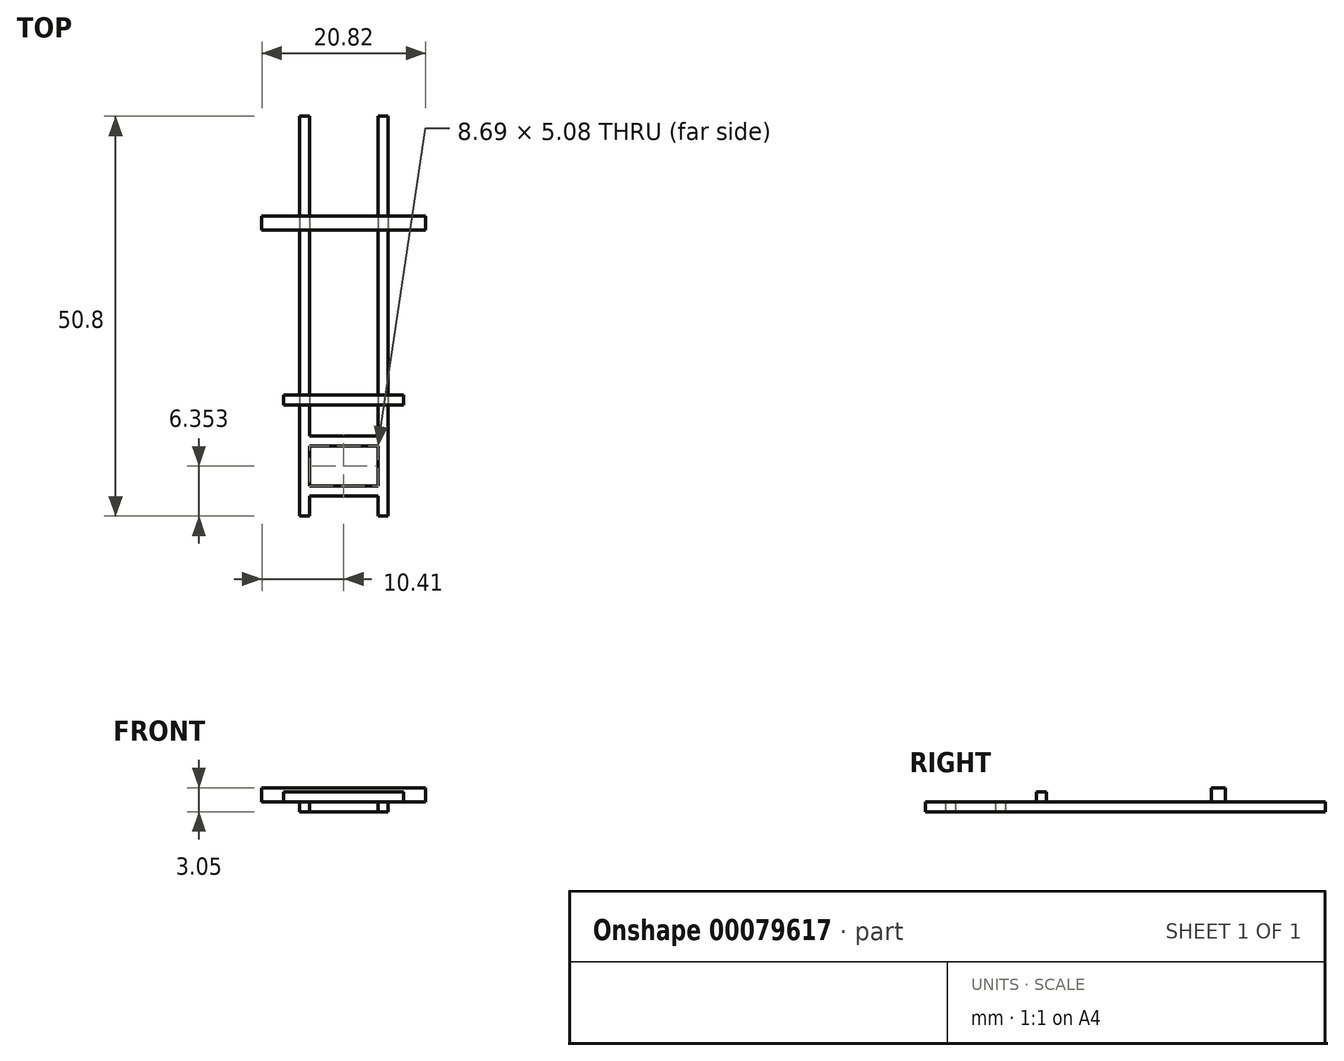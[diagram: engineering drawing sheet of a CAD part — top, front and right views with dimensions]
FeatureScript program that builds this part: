
annotation { "Feature Type Name" : "Feature", "Feature Type Description" : "" }
export const myFeature = defineFeature(function(context is Context, id is Id, definition is map)
    precondition{}
    {
        {
            var Q0;
            Q0=qCreatedBy(makeId("Top.planeOp"),FACE);
            var sketch = newSketch(context, id + "F0", { "sketchPlane" : qUnion([Q0])});
            skLineSegment(sketch, "E0.bottom", {"start": v(-5.61, 6.98) * mm, "end": v(-4.34, 6.98) * mm});
            skLineSegment(sketch, "E0.top", {"start": v(-5.61, -43.82) * mm, "end": v(-4.34, -43.82) * mm});
            skLineSegment(sketch, "E0.left", {"start": v(-5.61, 6.98) * mm, "end": v(-5.61, -43.82) * mm});
            skLineSegment(sketch, "E0.right", {"start": v(-4.34, 6.98) * mm, "end": v(-4.34, -43.82) * mm});
            skLineSegment(sketch, "E1.bottom", {"start": v(4.34, 6.98) * mm, "end": v(5.61, 6.98) * mm});
            skLineSegment(sketch, "E1.top", {"start": v(4.34, -43.82) * mm, "end": v(5.61, -43.82) * mm});
            skLineSegment(sketch, "E1.left", {"start": v(4.34, 6.98) * mm, "end": v(4.34, -43.82) * mm});
            skLineSegment(sketch, "E1.right", {"start": v(5.61, 6.98) * mm, "end": v(5.61, -43.82) * mm});
            skLineSegment(sketch, "E2", {"start": v(-4.34, -41.28) * mm, "end": v(4.34, -41.28) * mm});
            skLineSegment(sketch, "E3", {"start": v(-4.34, -40) * mm, "end": v(4.34, -40) * mm});
            skLineSegment(sketch, "E4", {"start": v(-4.34, -34.93) * mm, "end": v(4.34, -34.93) * mm});
            skLineSegment(sketch, "E5", {"start": v(-4.34, -33.66) * mm, "end": v(4.34, -33.66) * mm});
            skSolve(sketch);
        }
        {
            var Q0;
            Q0 = qSketchRegion(id + "F0", true);
            extrude(context, id + "F1", {"entities" : qUnion([Q0]), "depth" : 1.27 * mm});
        }
        {
            var Q0;
            Q0=makeQuery(id+"F1.opExtrude","CAP_FACE",FACE,{"disambiguationData":[OSD([sQuery(id+"F0.wireOp",EDGE,"E0.bottom"),sQuery(id+"F0.wireOp",EDGE,"E0.top"),sQuery(id+"F0.wireOp",EDGE,"E0.left"),sQuery(id+"F0.wireOp",EDGE,"E0.right"),sQuery(id+"F0.wireOp",EDGE,"E1.bottom"),sQuery(id+"F0.wireOp",EDGE,"E1.top"),sQuery(id+"F0.wireOp",EDGE,"E1.left"),sQuery(id+"F0.wireOp",EDGE,"E1.right"),sQuery(id+"F0.wireOp",EDGE,"E2"),sQuery(id+"F0.wireOp",EDGE,"E3"),sQuery(id+"F0.wireOp",EDGE,"E4"),sQuery(id+"F0.wireOp",EDGE,"E5")])],"isStart":false});
            var sketch = newSketch(context, id + "F2", { "sketchPlane" : qUnion([Q0])});
            skLineSegment(sketch, "E6.bottom", {"start": v(-10.41, -5.72) * mm, "end": v(10.41, -5.72) * mm});
            skLineSegment(sketch, "E6.top", {"start": v(-10.41, -7.5) * mm, "end": v(10.41, -7.5) * mm});
            skLineSegment(sketch, "E6.left", {"start": v(-10.41, -5.72) * mm, "end": v(-10.41, -7.5) * mm});
            skLineSegment(sketch, "E6.right", {"start": v(10.41, -5.72) * mm, "end": v(10.41, -7.5) * mm});
            skSolve(sketch);
        }
        {
            var Q0;
            Q0 = qSketchRegion(id + "F2", true);
            extrude(context, id + "F3", {"entities" : qUnion([Q0]), "operationType" : NewBodyOperationType.ADD, "depth" : 1.78 * mm});
        }
        {
            var Q0;
            {var subQ0=sQuery(id+"F0.wireOp",EDGE,"E1.right");var subQ1=sQuery(id+"F0.wireOp",EDGE,"E3");var subQ2=sQuery(id+"F0.wireOp",EDGE,"E1.left");var subQ3=sQuery(id+"F0.wireOp",EDGE,"E4");var subQ4=sQuery(id+"F0.wireOp",EDGE,"E1.top");var subQ5=sQuery(id+"F0.wireOp",EDGE,"E0.right");var subQ6=sQuery(id+"F0.wireOp",EDGE,"E0.top");var subQ7=sQuery(id+"F0.wireOp",EDGE,"E2");var subQ8=sQuery(id+"F0.wireOp",EDGE,"E1.bottom");var subQ9=sQuery(id+"F0.wireOp",EDGE,"E5");var subQ10=sQuery(id+"F0.wireOp",EDGE,"E0.left");var subQ11=sQuery(id+"F0.wireOp",EDGE,"E0.bottom");Q0=makeQuery(id+"F3.boolean.opBoolean","SPLIT",FACE,{"disambiguationData":[TD([makeQuery(id+"F1.opExtrude","SWEPT_FACE",FACE,{"disambiguationData":[OSD([subQ6])]})])],"derivedFrom":makeQuery(id+"F1.opExtrude","CAP_FACE",FACE,{"disambiguationData":[OSD([subQ11,subQ6,subQ10,subQ5,subQ8,subQ4,subQ2,subQ0,subQ7,subQ1,subQ3,subQ9])],"isStart":false})});}
            var sketch = newSketch(context, id + "F4", { "sketchPlane" : qUnion([Q0])});
            skLineSegment(sketch, "E7.bottom", {"start": v(-7.62, -28.46) * mm, "end": v(7.62, -28.46) * mm});
            skLineSegment(sketch, "E7.top", {"start": v(-7.62, -29.73) * mm, "end": v(7.62, -29.73) * mm});
            skLineSegment(sketch, "E7.left", {"start": v(-7.62, -28.46) * mm, "end": v(-7.62, -29.73) * mm});
            skLineSegment(sketch, "E7.right", {"start": v(7.62, -28.46) * mm, "end": v(7.62, -29.73) * mm});
            skSolve(sketch);
        }
        {
            var Q0;
            Q0 = qSketchRegion(id + "F4", true);
            extrude(context, id + "F5", {"entities" : qUnion([Q0]), "operationType" : NewBodyOperationType.ADD, "depth" : 1.27 * mm});
        }
    });
